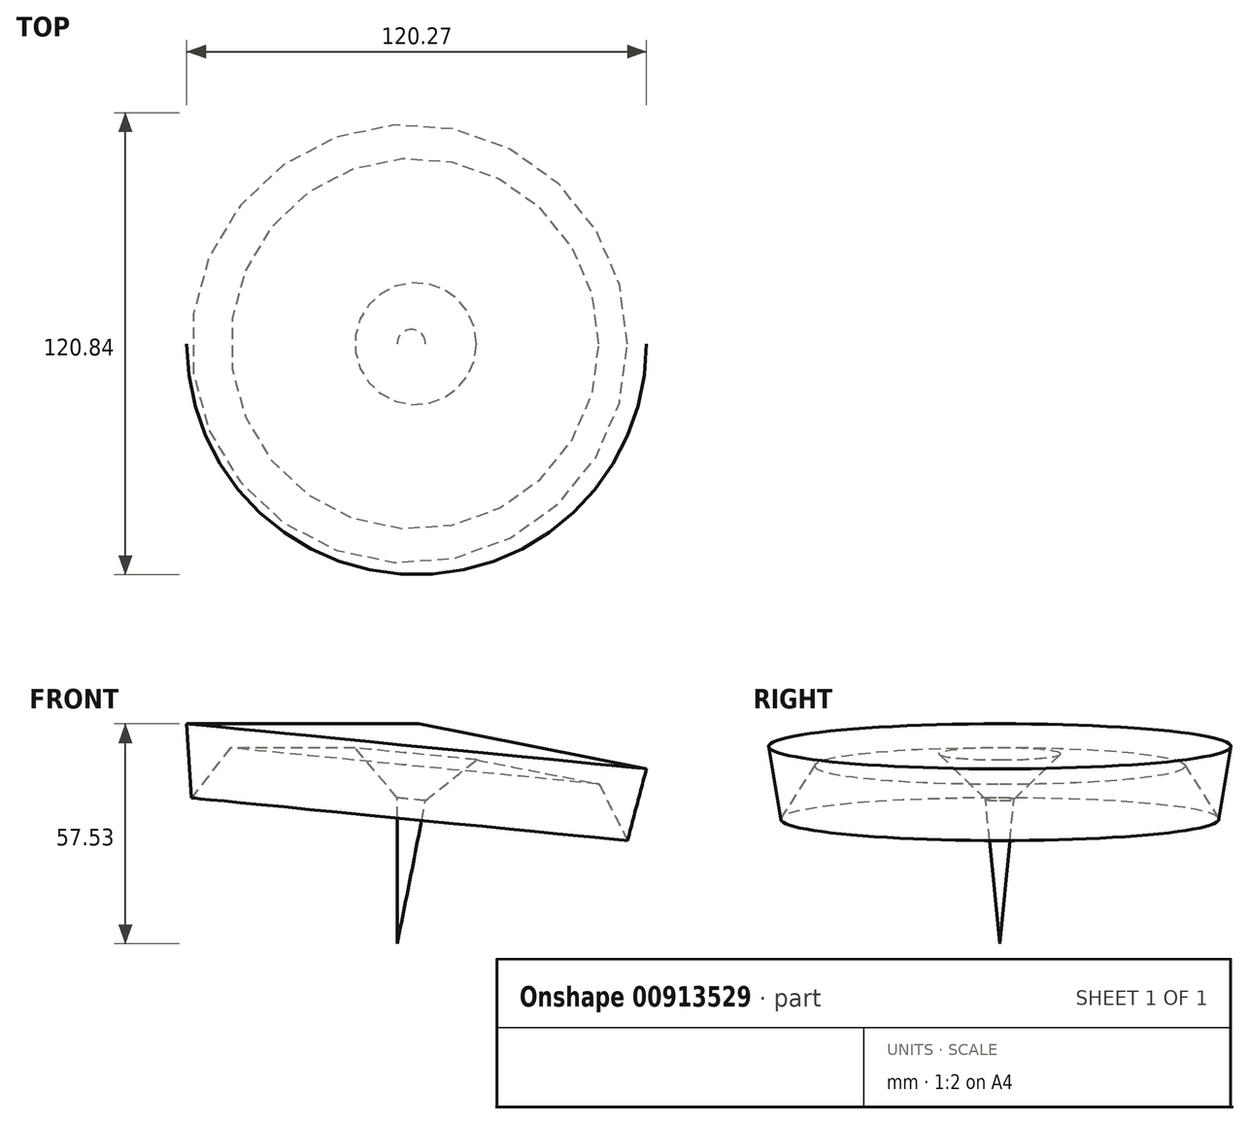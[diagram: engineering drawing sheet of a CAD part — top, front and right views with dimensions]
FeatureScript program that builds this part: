
annotation { "Feature Type Name" : "Feature", "Feature Type Description" : "" }
export const myFeature = defineFeature(function(context is Context, id is Id, definition is map)
    precondition{}
    {
        {
            var Q0;
            Q0=qCreatedBy(makeId("Front.planeOp"),FACE);
            var sketch = newSketch(context, id + "F0", { "sketchPlane" : qUnion([Q0])});
            skLineSegment(sketch, "E0", {"start": v(-60.71, 72.48) * mm, "end": v(0, 72.48) * mm});
            skLineSegment(sketch, "E1", {"start": v(0, 72.48) * mm, "end": v(-5.63, 14.95) * mm});
            skLineSegment(sketch, "E2", {"start": v(-5.63, 14.95) * mm, "end": v(-5.63, 53.13) * mm});
            skLineSegment(sketch, "E3", {"start": v(-5.63, 53.13) * mm, "end": v(-16.65, 66.18) * mm});
            skLineSegment(sketch, "E4", {"start": v(-16.65, 66.18) * mm, "end": v(-49.3, 66.18) * mm});
            skLineSegment(sketch, "E5", {"start": v(-49.3, 66.18) * mm, "end": v(-59.5, 53.13) * mm});
            skLineSegment(sketch, "E6", {"start": v(-60.71, 72.48) * mm, "end": v(-59.5, 53.13) * mm});
            skLineSegment(sketch, "E7", {"start": v(-5.63, 47.98) * mm, "end": v(-10.12, 53.13) * mm});
            skPoint(sketch, "E8.end.orphan", {"position": v(-33.78, 5.69) * mm});
            skPoint(sketch, "E9.end.orphan", {"position": v(-49.3, 5.69) * mm});
            skPoint(sketch, "E10.start.orphan", {"position": v(0, 0) * mm});
            skPoint(sketch, "E11.end.orphan", {"position": v(-10.12, 14.36) * mm});
            skPoint(sketch, "E12.start.orphan", {"position": v(-15.1, 72.48) * mm});
            skSolve(sketch);
        }
        {
            var Q0;
            Q0=makeQuery(id+"F0.imprint","IMPRINT",FACE,{"disambiguationData":[TD([[makeQuery(id+"F0.imprint","IMPRINT",EDGE,{"derivedFrom":sQuery(id+"F0.wireOp",EDGE,"E0")}),-1.0]])]});
            var Q1;
            Q1=sQuery(id+"F0.wireOp",EDGE,"E1");
            revolve(context, id + "F1", {"surfaceOperationType" : NewSurfaceOperationType.NEW, "entities" : qUnion([Q0]), "axis" : qUnion([Q1]), "revolveType" : RevolveType.FULL});
        }
    });
